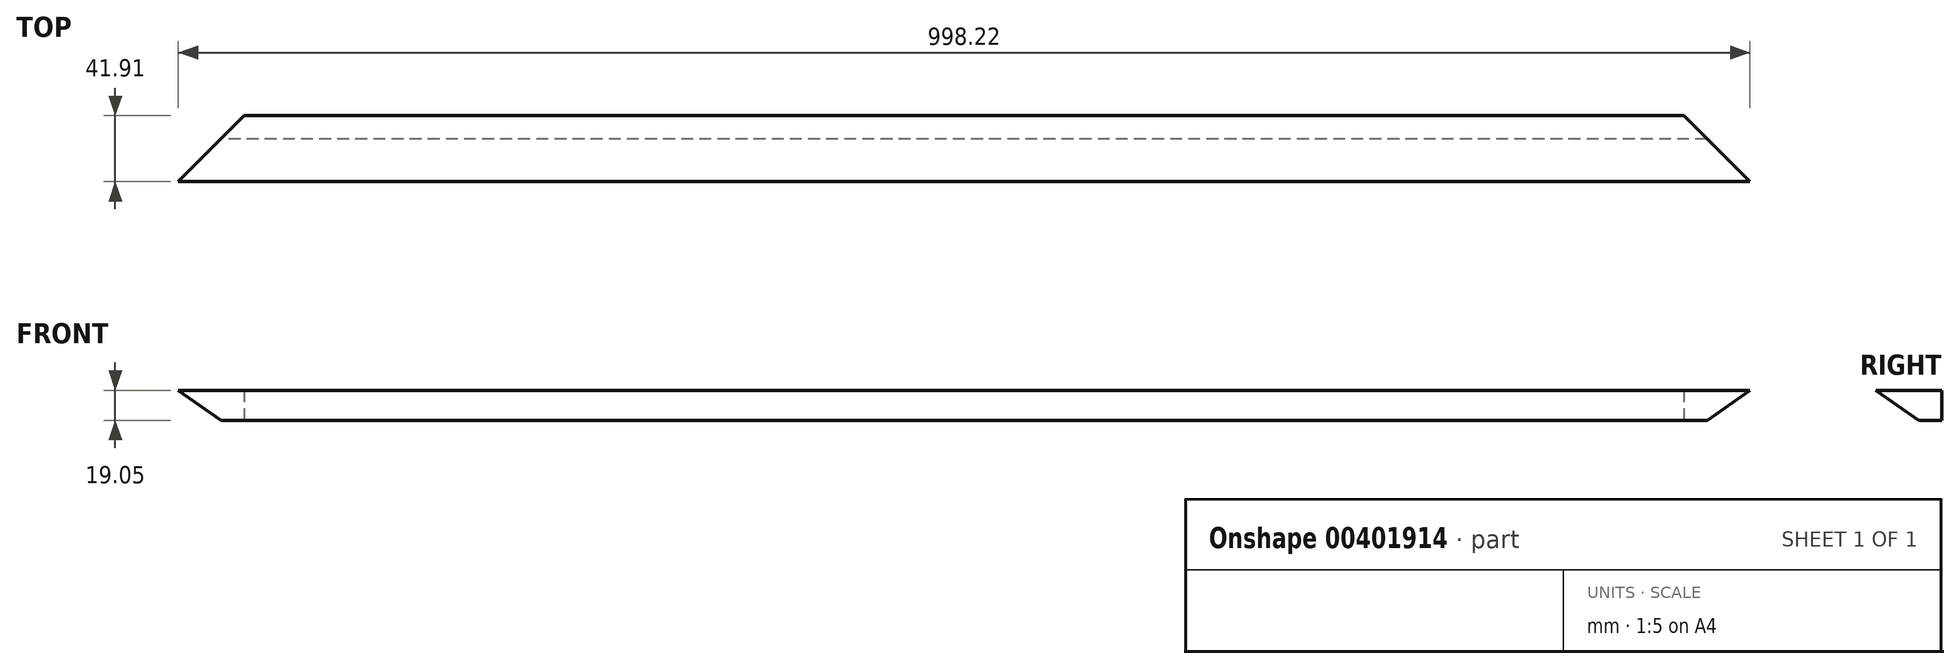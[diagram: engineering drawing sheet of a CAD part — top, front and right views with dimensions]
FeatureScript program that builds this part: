
annotation { "Feature Type Name" : "Feature", "Feature Type Description" : "" }
export const myFeature = defineFeature(function(context is Context, id is Id, definition is map)
    precondition{}
    {
        {
            var Q0;
            Q0=qCreatedBy(makeId("Right.planeOp"),FACE);
            var sketch = newSketch(context, id + "F0", { "sketchPlane" : qUnion([Q0])});
            skLineSegment(sketch, "E0.bottom", {"start": v(0, 19.05) * mm, "end": v(-41.91, 19.05) * mm});
            skLineSegment(sketch, "E0.top", {"start": v(0, 0) * mm, "end": v(-14.7, 0) * mm});
            skLineSegment(sketch, "E0.left", {"start": v(0, 19.05) * mm, "end": v(0, 0) * mm});
            skPoint(sketch, "E0.middle", {"position": v(0, 0) * mm});
            skLineSegment(sketch, "E1", {"start": v(-41.91, 19.05) * mm, "end": v(-14.7, 0) * mm});
            skSolve(sketch);
        }
        {
            var Q0;
            Q0=qSketchRegion(id+"F0",true);
            extrude(context, id + "F1", {"entities" : qUnion([Q0]), "depth" : 508 * mm, "hasSecondDirection" : true, "secondDirectionOppositeDirection" : true, "secondDirectionDepth" : 508 * mm});
        }
        {
            var Q0;
            Q0=qCreatedBy(makeId("Top.planeOp"),FACE);
            var sketch = newSketch(context, id + "F2", { "sketchPlane" : qUnion([Q0])});
            skLineSegment(sketch, "E2", {"start": v(-457.2, 0) * mm, "end": v(457.2, 0) * mm, "construction": true});
            skLineSegment(sketch, "E3", {"start": v(0, 0) * mm, "end": v(0, -153.4) * mm, "construction": true});
            skLineSegment(sketch, "E4", {"start": v(457.2, 0) * mm, "end": v(509.68, 0) * mm});
            skLineSegment(sketch, "E5", {"start": v(509.68, 0) * mm, "end": v(509.68, -52.48) * mm});
            skLineSegment(sketch, "E6", {"start": v(509.68, -52.48) * mm, "end": v(457.2, 0) * mm});
            skLineSegment(sketch, "E7.MirrorCS", {"start": v(-457.2, 0) * mm, "end": v(-509.68, 0) * mm});
            skLineSegment(sketch, "E8.MirrorCS", {"start": v(-509.68, 0) * mm, "end": v(-509.68, -52.48) * mm});
            skLineSegment(sketch, "E9.MirrorCS", {"start": v(-509.68, -52.48) * mm, "end": v(-457.2, 0) * mm});
            skSolve(sketch);
        }
        {
            var Q0;
            Q0=qSketchRegion(id+"F2",true);
            extrude(context, id + "F3", {"entities" : qUnion([Q0]), "operationType" : NewBodyOperationType.REMOVE, "endBound" : BoundingType.THROUGH_ALL, "depth" : 25.4 * mm});
        }
    });
